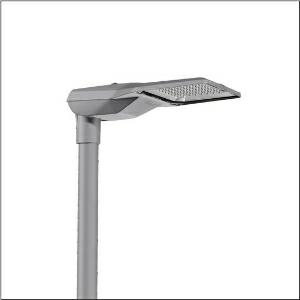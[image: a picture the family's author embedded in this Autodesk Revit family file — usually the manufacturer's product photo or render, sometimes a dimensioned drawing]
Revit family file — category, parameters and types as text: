
# Revit family: streetlight_sl_21_midi___p0_5a_5xe3v33s08lb_b536
name_source: partatom
category: Lighting Fixtures
units: mm (PartAtom-declared; Revit-internal decimal feet)

## family parameters
Cut with Voids When Loaded = No
Host = Face
Light Source = No
Part Type = Normal
Room Calculation Point = No
Round Connector Dimension = Use Diameter
Shared = No

## types (1)
- --- (1 x LED, 14100 lm, 99.6 W, 3000K)
    Apparent Load = 100 VA
    CIE Flux Codes = 37 73 96 100 100
    Color Rendering = 70
    Color Temperature = 3000K
    Default Elevation = 1800 mm
    Description = Streetlight SL 21 midi, mast luminaire, primary light control with lens, of PMMA, primary optical cover: cover, of toughened safety glass, transparent, light distribution: P0.5a, light emission: direct distribution, primary light characteristic: asymmetric, installation type: post-top, side-entry, LED, High Power LED, rated luminous flux: 14.100lm, luminous efficacy: 142lm/W, light colour: 730, colour temperature: 3000K, control gear: D4i, control: pre-setting: logarithmic dimming characteristic, flexible luminous flux parameterisation, time-dependent luminous flux control, constant luminous flux control, overheat protection, mains connection: 230..240V, AC, 50/60Hz, start of lifetime: 100W, end of service life: 102W, reduction: 46W, luminaire housing, of diecast aluminium, powder-coated, SITECO metallic grey (DB 702S), corrosivity category C5 high according to DIN EN ISO 12944, multi-level sealing system, sealing non-destructively replaceable, inclination adjustable: 0°, 5°, 10°, 15°, please order mast flange separately, length: 644mm, width: 335mm, height: 110mm, mast flange for spigot size: 42mm (side-entry): 5XC10008XM4, 60/48mm (side-entry/post-top): 5XC10108XM2, 76/60mm (side-entry/post-top): 5XC10108XM1, mounting height: 4..8m, Smart Interface above, protection rating (complete): IP66, insulation class (complete): insulation class II (safety insulation), certification: CE, ENEC, ENEC+, VDE, impact resistance: IK10, permissible operating ambient temperature for outdoor applications: -40..+50°C, standard-compliant lighting for roads and squares, packaging unit: 1 piece

Light Distribution: P0.5a
    Height = 111 mm
    Lamp = 1 x LED
    Lamp Light Flux = 14100 lm
    Lamp Power = 99.6 W
    Lamp count = 1
    Length = 644 mm
    Luminous efficacy = 142 lm/W
    Manufacturer = Siteco
    ModVariant = No
    Model = 5XE3V33S08LB
    Number of Poles = 1
    OnlyDefault = Yes
    Power Factor = 1
    Product Name = Streetlight SL 21 midi | P0.5a
    Product group = mast luminaire | pylon top
    ProductGroupID = 6100
    Protection Class = Protection class II
    Protection Degree = IP 66
    RLX_Detail_Level = 1
    RLX_Emergency_Light_Flux = 0 lm
    RLX_Emergency_Type = 0
    RLX_Emergency_Type_DB = No
    RlxData = <blob elided: 26353 chars, md5=d47299cf>
    Socket = socket
    Standby Power = 0 W
    System Light Flux = 14100 lm
    System Power = 100 W
    Type Comments = factory setting: luminous flux: 100 % | dim-lin: 254 | 1020 mA
    Type Image = l_1004302.jpg
    URL = http://relux.com
    VarID = @adj_032849
    Voltage = 0 V
    Weight = 0.00 kg
    Width = 336 mm

## geometry (parser evidence)
native form markers: Blend x4, Sweep x12
no freeform markers — native parametric forms only
